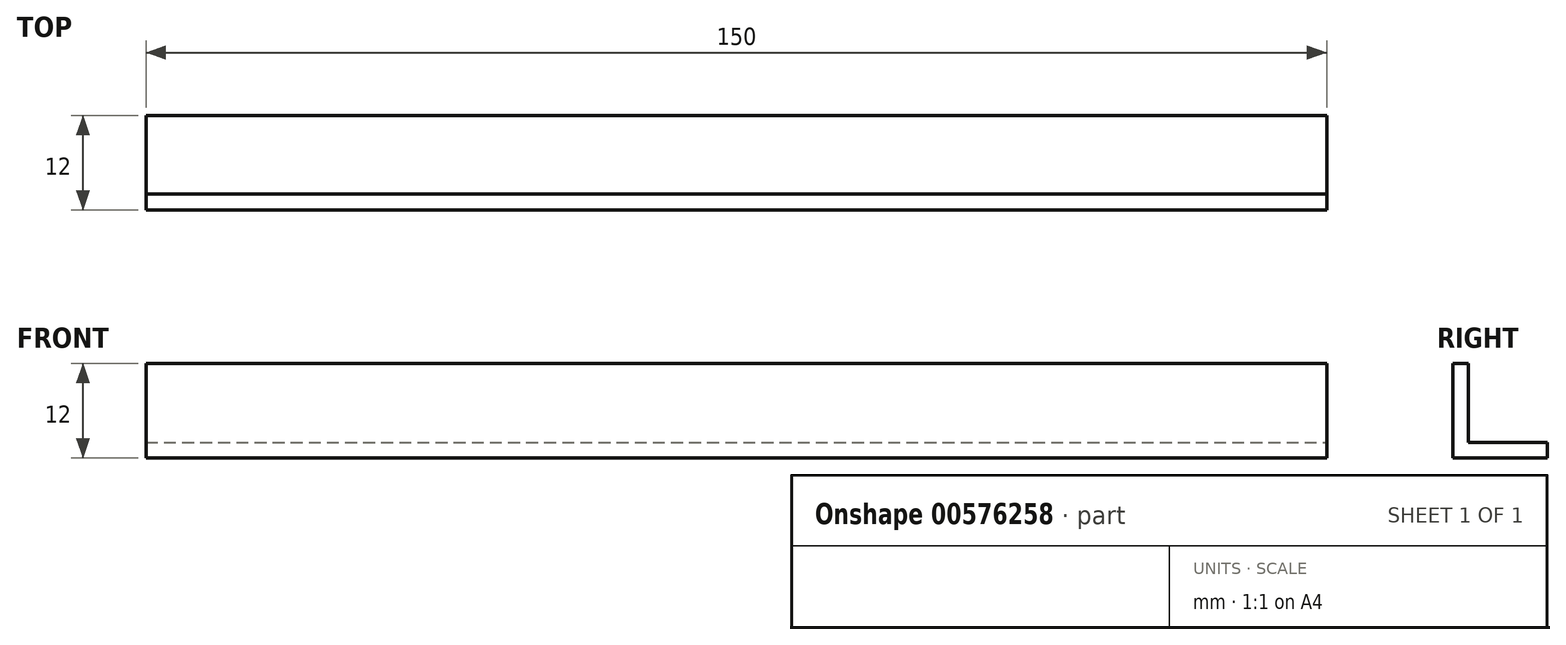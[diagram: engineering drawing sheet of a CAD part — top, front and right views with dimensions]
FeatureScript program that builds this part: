
annotation { "Feature Type Name" : "Feature", "Feature Type Description" : "" }
export const myFeature = defineFeature(function(context is Context, id is Id, definition is map)
    precondition{}
    {
        {
            var Q0;
            Q0=qCreatedBy(makeId("Top.planeOp"),FACE);
            var sketch = newSketch(context, id + "F0", { "sketchPlane" : qUnion([Q0])});
            skLineSegment(sketch, "E0", {"start": v(0, 0) * mm, "end": v(150, 0) * mm});
            skLineSegment(sketch, "E1", {"start": v(150, 0) * mm, "end": v(150, 10) * mm});
            skLineSegment(sketch, "E2", {"start": v(150, 10) * mm, "end": v(0, 10) * mm});
            skLineSegment(sketch, "E3", {"start": v(0, 10) * mm, "end": v(0, 0) * mm});
            skLineSegment(sketch, "E4", {"start": v(150, 0) * mm, "end": v(150, -2) * mm});
            skLineSegment(sketch, "E5", {"start": v(150, -2) * mm, "end": v(0, -2) * mm});
            skLineSegment(sketch, "E6", {"start": v(0, -2) * mm, "end": v(0, 0) * mm});
            skSolve(sketch);
        }
        {
            var Q0;
            Q0 = qSketchRegion(id + "F0", true);
            extrude(context, id + "F1", {"entities" : qUnion([Q0]), "oppositeDirection" : true, "depth" : 2 * mm, "offsetDistance" : 25 * mm});
        }
        {
            var Q0;
            Q0=makeQuery(id+"F0.imprint","IMPRINT",FACE,{"disambiguationData":[TD([[makeQuery(id+"F0.imprint","IMPRINT",EDGE,{"derivedFrom":sQuery(id+"F0.wireOp",EDGE,"E0")}),-1.0]])]});
            extrude(context, id + "F2", {"entities" : qUnion([Q0]), "operationType" : NewBodyOperationType.ADD, "depth" : 10 * mm, "offsetDistance" : 25 * mm});
        }
    });
